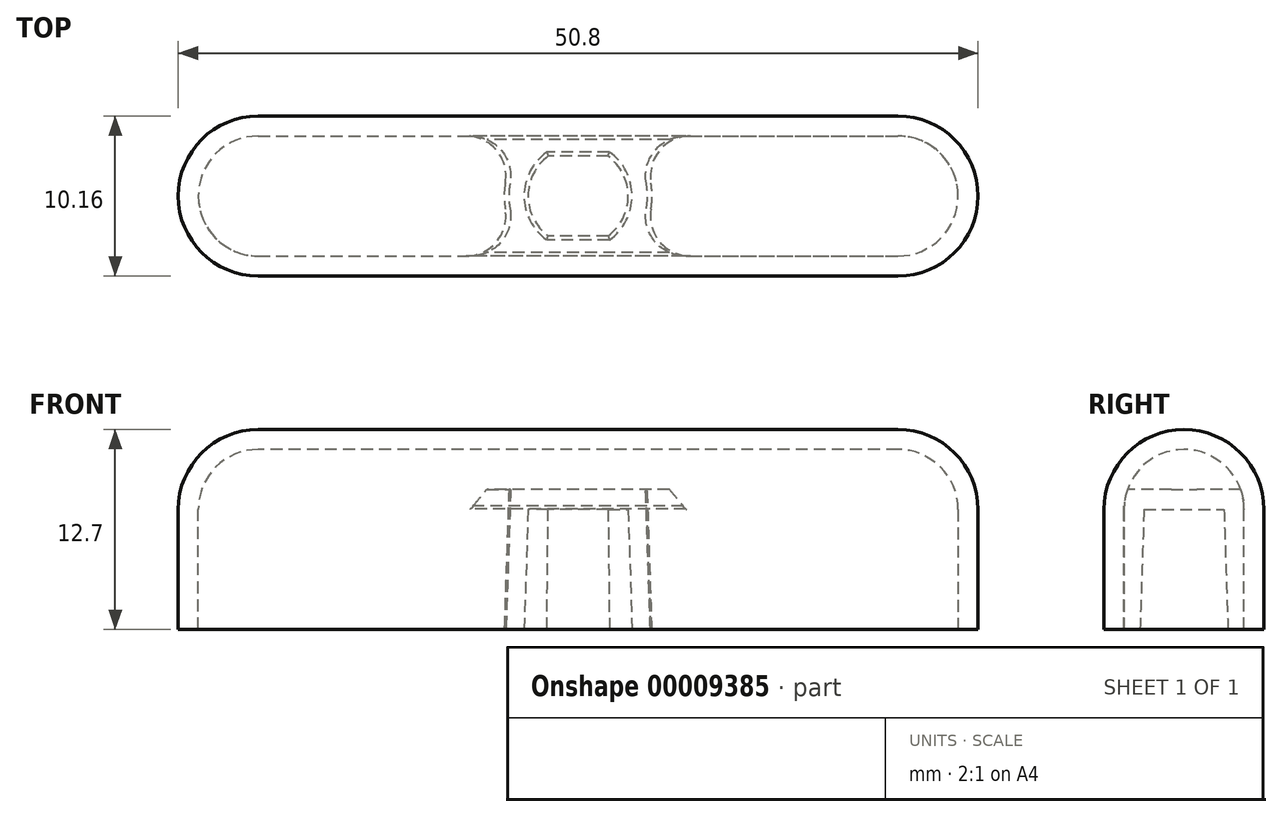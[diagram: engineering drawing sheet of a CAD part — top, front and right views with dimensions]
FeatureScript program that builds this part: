
annotation { "Feature Type Name" : "Feature", "Feature Type Description" : "" }
export const myFeature = defineFeature(function(context is Context, id is Id, definition is map)
    precondition{}
    {
        {
            var Q0;
            Q0=qCreatedBy(makeId("Top.planeOp"),FACE);
            var sketch = newSketch(context, id + "F0", { "sketchPlane" : qUnion([Q0])});
            skArc(sketch, "E0", {"start": v(-1.99, 2.8) * mm, "mid": v(-3.43, 0) * mm, "end": v(-1.99, -2.8) * mm, "construction": true});
            skLineSegment(sketch, "E1.rect.bottom", {"start": v(1.99, -2.8) * mm, "end": v(-1.99, -2.8) * mm, "construction": true});
            skLineSegment(sketch, "E1.rect.top", {"start": v(1.99, 2.8) * mm, "end": v(-1.99, 2.8) * mm, "construction": true});
            skLineSegment(sketch, "E1.rect.left", {"start": v(1.99, -2.8) * mm, "end": v(1.99, 2.8) * mm, "construction": true});
            skLineSegment(sketch, "E1.rect.right", {"start": v(-1.99, -2.8) * mm, "end": v(-1.99, 2.8) * mm, "construction": true});
            skArc(sketch, "E2.trimOffspring", {"start": v(1.99, -2.8) * mm, "mid": v(3.43, 0) * mm, "end": v(1.99, 2.8) * mm, "construction": true});
            skLineSegment(sketch, "E3.0", {"start": v(1.99, 2.8) * mm, "end": v(-1.99, 2.8) * mm});
            skArc(sketch, "E3.1", {"start": v(1.99, -2.8) * mm, "mid": v(3.43, 0) * mm, "end": v(1.99, 2.8) * mm});
            skLineSegment(sketch, "E3.2", {"start": v(1.99, -2.8) * mm, "end": v(-1.99, -2.8) * mm});
            skArc(sketch, "E3.3", {"start": v(-1.99, 2.8) * mm, "mid": v(-3.43, 0) * mm, "end": v(-1.99, -2.8) * mm});
            skSolve(sketch);
        }
        {
            var Q0;
            Q0=qCreatedBy(makeId("Top.planeOp"),FACE);
            var sketch = newSketch(context, id + "F1", { "sketchPlane" : qUnion([Q0])});
            skLineSegment(sketch, "E4.rect.bottom", {"start": v(-25.4, -5.08) * mm, "end": v(25.4, -5.08) * mm});
            skLineSegment(sketch, "E4.rect.top", {"start": v(-25.4, 5.08) * mm, "end": v(25.4, 5.08) * mm});
            skLineSegment(sketch, "E4.rect.left", {"start": v(-25.4, -5.08) * mm, "end": v(-25.4, 5.08) * mm});
            skLineSegment(sketch, "E4.rect.right", {"start": v(25.4, -5.08) * mm, "end": v(25.4, 5.08) * mm});
            skPoint(sketch, "E4.rect.middle", {"position": v(0, 0) * mm});
            skSolve(sketch);
        }
        {
            var Q0;
            Q0 = qSketchRegion(id + "F1", true);
            extrude(context, id + "F2", {"entities" : qUnion([Q0]), "depth" : 12.7 * mm});
        }
        {
            var Q0;
            Q0=makeQuery(id+"F2.opExtrude","CAP_EDGE",EDGE,{"disambiguationData":[OSD([sQuery(id+"F1.wireOp",EDGE,"E4.rect.left")])],"isStart":false});
            var Q1;
            Q1=makeQuery(id+"F2.opExtrude","SWEPT_EDGE",EDGE,{"disambiguationData":[OSD([sQuery(id+"F1.wireOp",EDGE,"E4.rect.bottom"),sQuery(id+"F1.wireOp",EDGE,"E4.rect.left")])]});
            var Q2;
            Q2=makeQuery(id+"F2.opExtrude","SWEPT_EDGE",EDGE,{"disambiguationData":[OSD([sQuery(id+"F1.wireOp",EDGE,"E4.rect.top"),sQuery(id+"F1.wireOp",EDGE,"E4.rect.left")])]});
            var Q3;
            Q3=makeQuery(id+"F2.opExtrude","CAP_EDGE",EDGE,{"disambiguationData":[OSD([sQuery(id+"F1.wireOp",EDGE,"E4.rect.right")])],"isStart":false});
            var Q4;
            Q4=makeQuery(id+"F2.opExtrude","SWEPT_EDGE",EDGE,{"disambiguationData":[OSD([sQuery(id+"F1.wireOp",EDGE,"E4.rect.bottom"),sQuery(id+"F1.wireOp",EDGE,"E4.rect.right")])]});
            var Q5;
            Q5=makeQuery(id+"F2.opExtrude","SWEPT_EDGE",EDGE,{"disambiguationData":[OSD([sQuery(id+"F1.wireOp",EDGE,"E4.rect.top"),sQuery(id+"F1.wireOp",EDGE,"E4.rect.right")])]});
            var Q6;
            Q6=makeQuery(id+"F2.opExtrude","CAP_EDGE",EDGE,{"disambiguationData":[OSD([sQuery(id+"F1.wireOp",EDGE,"E4.rect.bottom")])],"isStart":false});
            var Q7;
            Q7=makeQuery(id+"F2.opExtrude","CAP_EDGE",EDGE,{"disambiguationData":[OSD([sQuery(id+"F1.wireOp",EDGE,"E4.rect.top")])],"isStart":false});
            fillet(context, id + "F3", {"entities" : qUnion([Q0, Q1, Q2, Q3, Q4, Q5, Q6, Q7]), "radius" : 5.08 * mm, "tangentPropagation" : true, "allowEdgeOverflow" : false});
        }
        {
            var Q0;
            Q0=qCreatedBy(makeId("Top.planeOp"),FACE);
            cPlane(context, id + "F4", {"entities" : qUnion([Q0]), "cplaneType" : CPlaneType.OFFSET, "offset" : 7.62 * mm, "width" : 152.4 * mm, "height" : 152.4 * mm});
        }
        {
            var Q0;
            Q0=qCreatedBy(id+"F4.planeOp",FACE);
            var sketch = newSketch(context, id + "F5", { "sketchPlane" : qUnion([Q0])});
            skArc(sketch, "E5", {"start": v(-1.9, 2.54) * mm, "mid": v(-3.17, 0) * mm, "end": v(-1.9, -2.54) * mm});
            skLineSegment(sketch, "E6.rect.bottom", {"start": v(1.9, -2.54) * mm, "end": v(-1.9, -2.54) * mm});
            skLineSegment(sketch, "E6.rect.top", {"start": v(1.9, 2.54) * mm, "end": v(-1.9, 2.54) * mm});
            skLineSegment(sketch, "E6.rect.left", {"start": v(1.9, -2.54) * mm, "end": v(1.9, 2.54) * mm, "construction": true});
            skLineSegment(sketch, "E6.rect.right", {"start": v(-1.9, -2.54) * mm, "end": v(-1.9, 2.54) * mm, "construction": true});
            skArc(sketch, "E7.trimOffspring", {"start": v(1.9, -2.54) * mm, "mid": v(3.17, 0) * mm, "end": v(1.9, 2.54) * mm});
            skSolve(sketch);
        }
        {
            var Q1;
            Q1 = qSketchRegion(id + "F0", true);
            var Q2;
            Q2 = qSketchRegion(id + "F5", true);
            loft(context, id + "F6", {"operationType" : NewBodyOperationType.REMOVE, "sheetProfilesArray" : [{ "sheetProfileEntities" : qUnion([Q1]) }, { "sheetProfileEntities" : qUnion([Q2]) }]});
        }
        {
            var Q0;
            Q0=makeQuery(id+"F2.opExtrude","CAP_FACE",FACE,{"disambiguationData":[OSD([sQuery(id+"F1.wireOp",EDGE,"E4.rect.bottom"),sQuery(id+"F1.wireOp",EDGE,"E4.rect.top"),sQuery(id+"F1.wireOp",EDGE,"E4.rect.left"),sQuery(id+"F1.wireOp",EDGE,"E4.rect.right")])],"isStart":true});
            shell(context, id + "F7", {"entities" : qUnion([Q0]), "thickness" : 1.27 * mm});
        }
        {
            var Q0;
            Q0=makeQuery(id+"F7.opShell","TWEAK_EDGE",EDGE,{"derivedFrom":[makeQuery(id+"F2.opExtrude","SWEPT_FACE",FACE,{"disambiguationData":[OSD([sQuery(id+"F1.wireOp",EDGE,"E4.rect.bottom")])]}),makeQuery(id+"F6.boolean.opBoolean","COPY",FACE,{"derivedFrom":makeQuery(id+"F6.opLoft","SWEPT_FACE",FACE,{"disambiguationData":[OSD([sQuery(id+"F0.wireOp",EDGE,"E3.0"),sQuery(id+"F0.wireOp",EDGE,"E3.2"),sQuery(id+"F0.wireOp",EDGE,"E3.3"),sQuery(id+"F5.wireOp",EDGE,"E5"),sQuery(id+"F5.wireOp",EDGE,"E6.rect.bottom"),sQuery(id+"F5.wireOp",EDGE,"E6.rect.top")])]})})]});
            var Q1;
            Q1=makeQuery(id+"F7.opShell","TWEAK_EDGE",EDGE,{"derivedFrom":[makeQuery(id+"F2.opExtrude","SWEPT_FACE",FACE,{"disambiguationData":[OSD([sQuery(id+"F1.wireOp",EDGE,"E4.rect.bottom")])]}),makeQuery(id+"F6.boolean.opBoolean","COPY",FACE,{"derivedFrom":makeQuery(id+"F6.opLoft","SWEPT_FACE",FACE,{"disambiguationData":[OSD([sQuery(id+"F0.wireOp",EDGE,"E3.0"),sQuery(id+"F0.wireOp",EDGE,"E3.1"),sQuery(id+"F0.wireOp",EDGE,"E3.2"),sQuery(id+"F5.wireOp",EDGE,"E6.rect.bottom"),sQuery(id+"F5.wireOp",EDGE,"E6.rect.top"),sQuery(id+"F5.wireOp",EDGE,"E7.trimOffspring")])]})})]});
            var Q2;
            Q2=makeQuery(id+"F7.opShell","TWEAK_EDGE",EDGE,{"derivedFrom":[makeQuery(id+"F2.opExtrude","SWEPT_FACE",FACE,{"disambiguationData":[OSD([sQuery(id+"F1.wireOp",EDGE,"E4.rect.top")])]}),makeQuery(id+"F6.boolean.opBoolean","COPY",FACE,{"derivedFrom":makeQuery(id+"F6.opLoft","SWEPT_FACE",FACE,{"disambiguationData":[OSD([sQuery(id+"F0.wireOp",EDGE,"E3.0"),sQuery(id+"F0.wireOp",EDGE,"E3.1"),sQuery(id+"F0.wireOp",EDGE,"E3.2"),sQuery(id+"F5.wireOp",EDGE,"E6.rect.bottom"),sQuery(id+"F5.wireOp",EDGE,"E6.rect.top"),sQuery(id+"F5.wireOp",EDGE,"E7.trimOffspring")])]})})]});
            var Q3;
            Q3=makeQuery(id+"F7.opShell","TWEAK_EDGE",EDGE,{"derivedFrom":[makeQuery(id+"F2.opExtrude","SWEPT_FACE",FACE,{"disambiguationData":[OSD([sQuery(id+"F1.wireOp",EDGE,"E4.rect.top")])]}),makeQuery(id+"F6.boolean.opBoolean","COPY",FACE,{"derivedFrom":makeQuery(id+"F6.opLoft","SWEPT_FACE",FACE,{"disambiguationData":[OSD([sQuery(id+"F0.wireOp",EDGE,"E3.0"),sQuery(id+"F0.wireOp",EDGE,"E3.2"),sQuery(id+"F0.wireOp",EDGE,"E3.3"),sQuery(id+"F5.wireOp",EDGE,"E5"),sQuery(id+"F5.wireOp",EDGE,"E6.rect.bottom"),sQuery(id+"F5.wireOp",EDGE,"E6.rect.top")])]})})]});
            fillet(context, id + "F8", {"entities" : qUnion([Q0, Q1, Q2, Q3]), "radius" : 2.54 * mm, "allowEdgeOverflow" : false});
        }
    });
